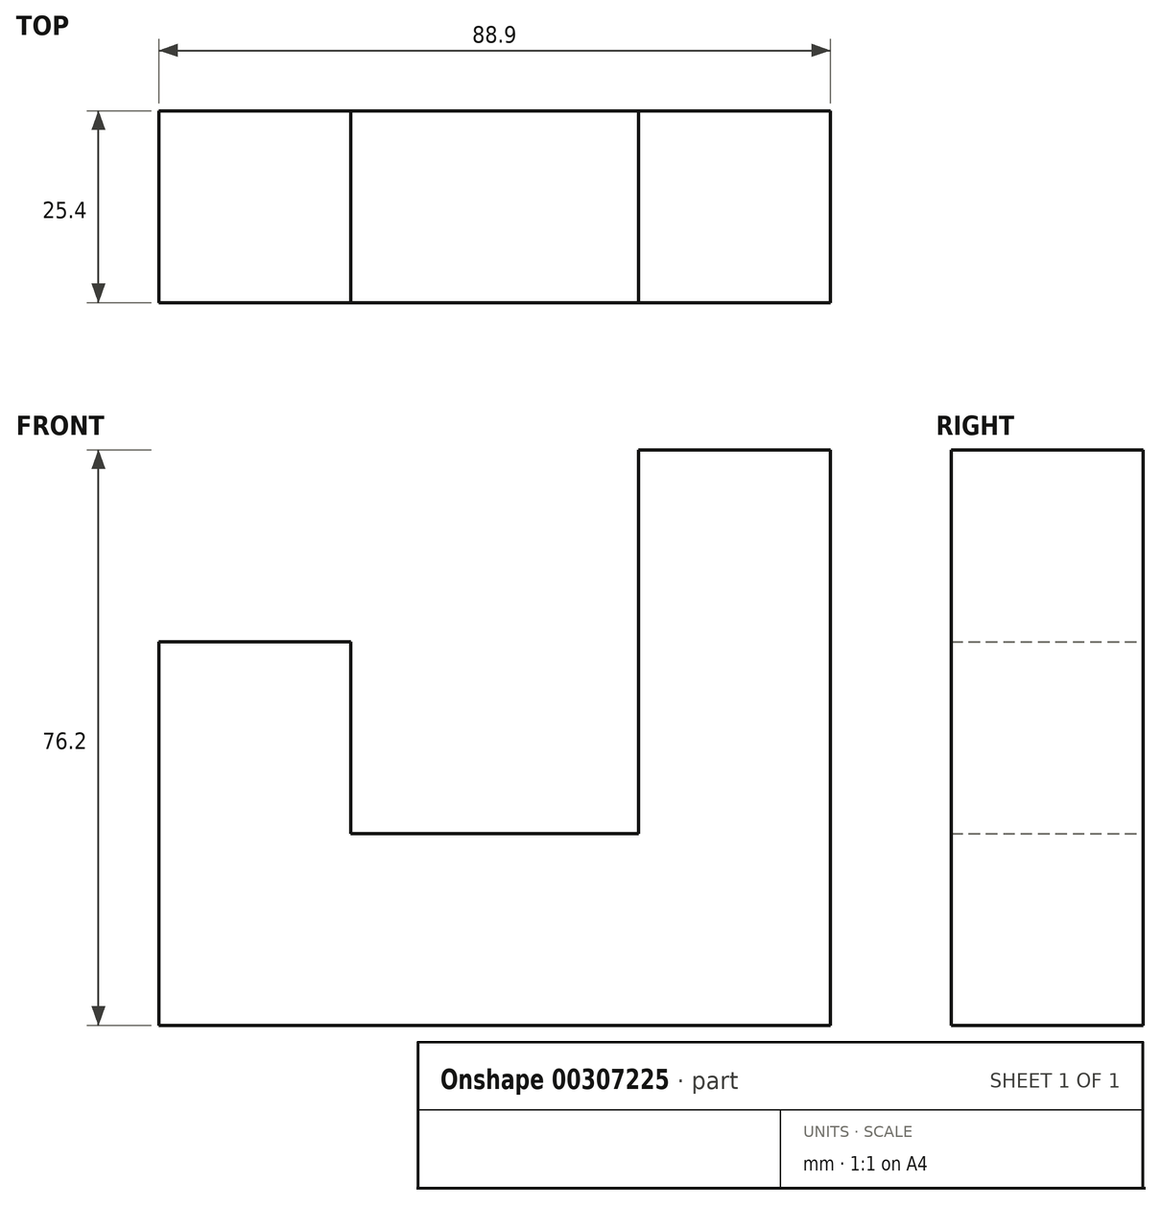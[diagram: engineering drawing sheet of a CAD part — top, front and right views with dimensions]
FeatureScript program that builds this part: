
annotation { "Feature Type Name" : "Feature", "Feature Type Description" : "" }
export const myFeature = defineFeature(function(context is Context, id is Id, definition is map)
    precondition{}
    {
        {
            var Q0;
            Q0=qCreatedBy(makeId("Front.planeOp"),FACE);
            var sketch = newSketch(context, id + "F0", { "sketchPlane" : qUnion([Q0])});
            skLineSegment(sketch, "E0", {"start": v(-30.7, -33.1) * mm, "end": v(58.2, -33.1) * mm});
            skLineSegment(sketch, "E1", {"start": v(58.2, -33.1) * mm, "end": v(58.2, 43.1) * mm});
            skLineSegment(sketch, "E2", {"start": v(58.2, 43.1) * mm, "end": v(32.8, 43.1) * mm});
            skLineSegment(sketch, "E3", {"start": v(32.8, 43.1) * mm, "end": v(32.8, -7.7) * mm});
            skLineSegment(sketch, "E4", {"start": v(32.8, -7.7) * mm, "end": v(-5.3, -7.7) * mm});
            skLineSegment(sketch, "E5", {"start": v(-5.3, -7.7) * mm, "end": v(-5.3, 17.7) * mm});
            skLineSegment(sketch, "E6", {"start": v(-5.3, 17.7) * mm, "end": v(-30.7, 17.7) * mm});
            skLineSegment(sketch, "E7", {"start": v(-30.7, 17.7) * mm, "end": v(-30.7, -33.1) * mm});
            skSolve(sketch);
        }
        {
            var Q0;
            Q0=makeQuery(id+"F0.imprint","IMPRINT",FACE,{"disambiguationData":[TD([[makeQuery(id+"F0.imprint","IMPRINT",EDGE,{"derivedFrom":sQuery(id+"F0.wireOp",EDGE,"E0")}),1.0]])]});
            extrude(context, id + "F1", {"entities" : qUnion([Q0]), "depth" : 25.4 * mm});
        }
    });
